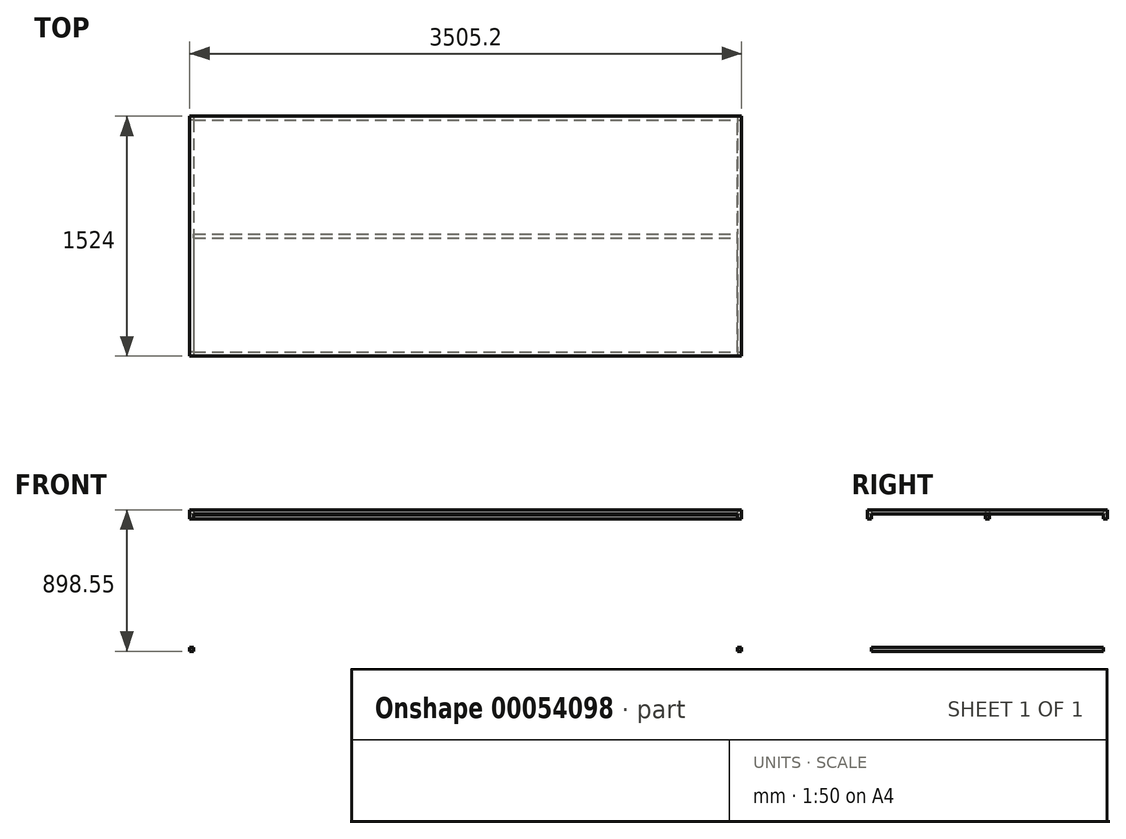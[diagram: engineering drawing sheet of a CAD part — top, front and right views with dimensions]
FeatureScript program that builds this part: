
annotation { "Feature Type Name" : "Feature", "Feature Type Description" : "" }
export const myFeature = defineFeature(function(context is Context, id is Id, definition is map)
    precondition{}
    {
        {
            var Q0;
            Q0=qCreatedBy(makeId("Top.planeOp"),FACE);
            var sketch = newSketch(context, id + "F0", { "sketchPlane" : qUnion([Q0])});
            skLineSegment(sketch, "E0.rect.bottom", {"start": v(-1752.6, 762) * mm, "end": v(1752.6, 762) * mm});
            skLineSegment(sketch, "E0.rect.top", {"start": v(-1752.6, -762) * mm, "end": v(1752.6, -762) * mm});
            skLineSegment(sketch, "E0.rect.left", {"start": v(-1752.6, 762) * mm, "end": v(-1752.6, -762) * mm});
            skLineSegment(sketch, "E0.rect.right", {"start": v(1752.6, 762) * mm, "end": v(1752.6, -762) * mm});
            skPoint(sketch, "E0.rect.middle", {"position": v(0, 0) * mm});
            skLineSegment(sketch, "E1.0", {"start": v(-1727.2, 736.6) * mm, "end": v(1727.2, 736.6) * mm});
            skLineSegment(sketch, "E1.1", {"start": v(-1727.2, 736.6) * mm, "end": v(-1727.2, -736.6) * mm});
            skLineSegment(sketch, "E1.2", {"start": v(-1727.2, -736.6) * mm, "end": v(1727.2, -736.6) * mm});
            skLineSegment(sketch, "E1.3", {"start": v(1727.2, 736.6) * mm, "end": v(1727.2, -736.6) * mm});
            skLineSegment(sketch, "E2", {"start": v(-1727.2, 0) * mm, "end": v(1727.2, 0) * mm, "construction": true});
            skLineSegment(sketch, "E3.0", {"start": v(-1727.2, -12.7) * mm, "end": v(1727.2, -12.7) * mm});
            skLineSegment(sketch, "E4.0", {"start": v(-1727.2, 12.7) * mm, "end": v(1727.2, 12.7) * mm});
            skSolve(sketch);
        }
        {
            var Q0;
            {var subQ0=sQuery(id+"F0.wireOp",EDGE,"E3.0");Q0=makeQuery(id+"F0.imprint","IMPRINT",FACE,{"disambiguationData":[TD([[makeQuery(id+"F0.imprint","IMPRINT",EDGE,{"derivedFrom":subQ0}),1.0]])]});}
            var Q1;
            Q1=makeQuery(id+"F0.imprint","IMPRINT",FACE,{"disambiguationData":[TD([[makeQuery(id+"F0.imprint","IMPRINT",EDGE,{"derivedFrom":sQuery(id+"F0.wireOp",EDGE,"E0.rect.bottom")}),-1.0]])]});
            extrude(context, id + "F1", {"entities" : qUnion([Q0, Q1]), "depth" : 25.4 * mm});
        }
        {
            var Q0;
            Q0=makeQuery(id+"F1.opExtrude","CAP_FACE",FACE,{"disambiguationData":[OSD([sQuery(id+"F0.wireOp",EDGE,"E0.rect.bottom"),sQuery(id+"F0.wireOp",EDGE,"E0.rect.top"),sQuery(id+"F0.wireOp",EDGE,"E0.rect.left"),sQuery(id+"F0.wireOp",EDGE,"E0.rect.right"),sQuery(id+"F0.wireOp",EDGE,"E1.0"),sQuery(id+"F0.wireOp",EDGE,"E1.1"),sQuery(id+"F0.wireOp",EDGE,"E1.2"),sQuery(id+"F0.wireOp",EDGE,"E1.3"),sQuery(id+"F0.wireOp",EDGE,"E3.0"),sQuery(id+"F0.wireOp",EDGE,"E4.0")])],"isStart":true});
            var sketch = newSketch(context, id + "F2", { "sketchPlane" : qUnion([Q0])});
            skLineSegment(sketch, "E5.bottom", {"start": v(-1727.2, 736.6) * mm, "end": v(-1752.6, 736.6) * mm});
            skLineSegment(sketch, "E5.top", {"start": v(-1727.2, 762) * mm, "end": v(-1752.6, 762) * mm});
            skLineSegment(sketch, "E5.left", {"start": v(-1727.2, 736.6) * mm, "end": v(-1727.2, 762) * mm});
            skLineSegment(sketch, "E5.right", {"start": v(-1752.6, 736.6) * mm, "end": v(-1752.6, 762) * mm});
            skLineSegment(sketch, "E6.bottom", {"start": v(-1752.6, -762) * mm, "end": v(-1727.2, -762) * mm});
            skLineSegment(sketch, "E6.top", {"start": v(-1752.6, -736.6) * mm, "end": v(-1727.2, -736.6) * mm});
            skLineSegment(sketch, "E6.left", {"start": v(-1752.6, -762) * mm, "end": v(-1752.6, -736.6) * mm});
            skLineSegment(sketch, "E6.right", {"start": v(-1727.2, -762) * mm, "end": v(-1727.2, -736.6) * mm});
            skLineSegment(sketch, "E7.bottom", {"start": v(1752.6, -762) * mm, "end": v(1727.2, -762) * mm});
            skLineSegment(sketch, "E7.top", {"start": v(1752.6, -736.6) * mm, "end": v(1727.2, -736.6) * mm});
            skLineSegment(sketch, "E7.left", {"start": v(1752.6, -762) * mm, "end": v(1752.6, -736.6) * mm});
            skLineSegment(sketch, "E7.right", {"start": v(1727.2, -762) * mm, "end": v(1727.2, -736.6) * mm});
            skLineSegment(sketch, "E8.bottom", {"start": v(1727.2, 736.6) * mm, "end": v(1752.6, 736.6) * mm});
            skLineSegment(sketch, "E8.top", {"start": v(1727.2, 762) * mm, "end": v(1752.6, 762) * mm});
            skLineSegment(sketch, "E8.left", {"start": v(1727.2, 736.6) * mm, "end": v(1727.2, 762) * mm});
            skLineSegment(sketch, "E8.right", {"start": v(1752.6, 736.6) * mm, "end": v(1752.6, 762) * mm});
            skSolve(sketch);
        }
        {
            var Q0;
            Q0 = qSketchRegion(id + "F2", true);
            extrude(context, id + "F3", {"entities" : qUnion([Q0]), "operationType" : NewBodyOperationType.ADD, "depth" : (29 + 5 + (3 / 8)) * mm});
        }
        {
            var Q0;
            Q0=makeQuery(id+"F3.boolean.opBoolean","MERGE",FACE,{"derivedFrom":[makeQuery(id+"F1.opExtrude","SWEPT_FACE",FACE,{"disambiguationData":[OSD([sQuery(id+"F0.wireOp",EDGE,"E0.rect.right")])]}),makeQuery(id+"F3.opExtrude","SWEPT_FACE",FACE,{"disambiguationData":[OSD([sQuery(id+"F2.wireOp",EDGE,"E7.left")])]}),makeQuery(id+"F3.opExtrude","SWEPT_FACE",FACE,{"disambiguationData":[OSD([sQuery(id+"F2.wireOp",EDGE,"E8.right")])]})]});
            var sketch = newSketch(context, id + "F4", { "sketchPlane" : qUnion([Q0])});
            skLineSegment(sketch, "E9.bottom", {"start": v(-736.6, -873.12) * mm, "end": v(736.6, -873.12) * mm});
            skLineSegment(sketch, "E9.top", {"start": v(-736.6, -847.73) * mm, "end": v(736.6, -847.73) * mm});
            skLineSegment(sketch, "E9.left", {"start": v(-736.6, -873.12) * mm, "end": v(-736.6, -847.73) * mm});
            skLineSegment(sketch, "E9.right", {"start": v(736.6, -873.12) * mm, "end": v(736.6, -847.73) * mm});
            skSolve(sketch);
        }
        {
            var Q0;
            Q0 = qSketchRegion(id + "F4", true);
            extrude(context, id + "F5", {"entities" : qUnion([Q0]), "operationType" : NewBodyOperationType.ADD, "oppositeDirection" : true, "depth" : 25.4 * mm});
        }
        {
            var Q0;
            Q0=makeQuery(id+"F3.boolean.opBoolean","MERGE",FACE,{"derivedFrom":[makeQuery(id+"F1.opExtrude","SWEPT_FACE",FACE,{"disambiguationData":[OSD([sQuery(id+"F0.wireOp",EDGE,"E0.rect.left")])]}),makeQuery(id+"F3.opExtrude","SWEPT_FACE",FACE,{"disambiguationData":[OSD([sQuery(id+"F2.wireOp",EDGE,"E5.right")])]}),makeQuery(id+"F3.opExtrude","SWEPT_FACE",FACE,{"disambiguationData":[OSD([sQuery(id+"F2.wireOp",EDGE,"E6.left")])]})]});
            var sketch = newSketch(context, id + "F6", { "sketchPlane" : qUnion([Q0])});
            skLineSegment(sketch, "E10.bottom", {"start": v(-736.6, -873.12) * mm, "end": v(736.6, -873.12) * mm});
            skLineSegment(sketch, "E10.top", {"start": v(-736.6, -847.73) * mm, "end": v(736.6, -847.73) * mm});
            skLineSegment(sketch, "E10.left", {"start": v(-736.6, -873.12) * mm, "end": v(-736.6, -847.73) * mm});
            skLineSegment(sketch, "E10.right", {"start": v(736.6, -873.12) * mm, "end": v(736.6, -847.73) * mm});
            skSolve(sketch);
        }
        {
            var Q0;
            Q0 = qSketchRegion(id + "F6", true);
            extrude(context, id + "F7", {"entities" : qUnion([Q0]), "operationType" : NewBodyOperationType.ADD, "oppositeDirection" : true, "depth" : 25.4 * mm});
        }
        {
            var Q0;
            Q0=makeQuery(id+"F7.boolean.opBoolean","MERGE",FACE,{"derivedFrom":[makeQuery(id+"F3.opExtrude","CAP_FACE",FACE,{"disambiguationData":[OSD([sQuery(id+"F2.wireOp",EDGE,"E5.bottom"),sQuery(id+"F2.wireOp",EDGE,"E5.top"),sQuery(id+"F2.wireOp",EDGE,"E5.left"),sQuery(id+"F2.wireOp",EDGE,"E5.right")])],"isStart":false}),makeQuery(id+"F3.opExtrude","CAP_FACE",FACE,{"disambiguationData":[OSD([sQuery(id+"F2.wireOp",EDGE,"E6.bottom"),sQuery(id+"F2.wireOp",EDGE,"E6.top"),sQuery(id+"F2.wireOp",EDGE,"E6.left"),sQuery(id+"F2.wireOp",EDGE,"E6.right")])],"isStart":false}),makeQuery(id+"F7.opExtrude","SWEPT_FACE",FACE,{"disambiguationData":[OSD([sQuery(id+"F6.wireOp",EDGE,"E10.bottom")])]})]});
            var sketch = newSketch(context, id + "F8", { "sketchPlane" : qUnion([Q0])});
            skLineSegment(sketch, "E11.bottom", {"start": v(-1727.2, 12.7) * mm, "end": v(1727.2, 12.7) * mm});
            skLineSegment(sketch, "E11.top", {"start": v(-1727.2, -12.7) * mm, "end": v(1727.2, -12.7) * mm});
            skLineSegment(sketch, "E11.left", {"start": v(-1727.2, 12.7) * mm, "end": v(-1727.2, -12.7) * mm});
            skLineSegment(sketch, "E11.right", {"start": v(1727.2, 12.7) * mm, "end": v(1727.2, -12.7) * mm});
            skSolve(sketch);
        }
        {
            var Q0;
            Q0 = qSketchRegion(id + "F8", true);
            extrude(context, id + "F9", {"entities" : qUnion([Q0]), "operationType" : NewBodyOperationType.ADD, "oppositeDirection" : true, "depth" : 25.4 * mm});
        }
        {
            var Q0;
            Q0=makeQuery(id+"F1.opExtrude","CAP_FACE",FACE,{"disambiguationData":[OSD([sQuery(id+"F0.wireOp",EDGE,"E0.rect.bottom"),sQuery(id+"F0.wireOp",EDGE,"E0.rect.top"),sQuery(id+"F0.wireOp",EDGE,"E0.rect.left"),sQuery(id+"F0.wireOp",EDGE,"E0.rect.right"),sQuery(id+"F0.wireOp",EDGE,"E1.0"),sQuery(id+"F0.wireOp",EDGE,"E1.1"),sQuery(id+"F0.wireOp",EDGE,"E1.2"),sQuery(id+"F0.wireOp",EDGE,"E1.3"),sQuery(id+"F0.wireOp",EDGE,"E3.0"),sQuery(id+"F0.wireOp",EDGE,"E4.0")])],"isStart":false});
            var sketch = newSketch(context, id + "F10", { "sketchPlane" : qUnion([Q0])});
            skLineSegment(sketch, "E12.bottom", {"start": v(1752.6, 762) * mm, "end": v(-1752.6, 762) * mm});
            skLineSegment(sketch, "E12.top", {"start": v(1752.6, -762) * mm, "end": v(-1752.6, -762) * mm});
            skLineSegment(sketch, "E12.left", {"start": v(1752.6, 762) * mm, "end": v(1752.6, -762) * mm});
            skLineSegment(sketch, "E12.right", {"start": v(-1752.6, 762) * mm, "end": v(-1752.6, -762) * mm});
            skSolve(sketch);
        }
        {
            var Q0;
            Q0 = qSketchRegion(id + "F10", true);
            extrude(context, id + "F11", {"entities" : qUnion([Q0]), "depth" : 3 / 101.6 * mm});
        }
    });
